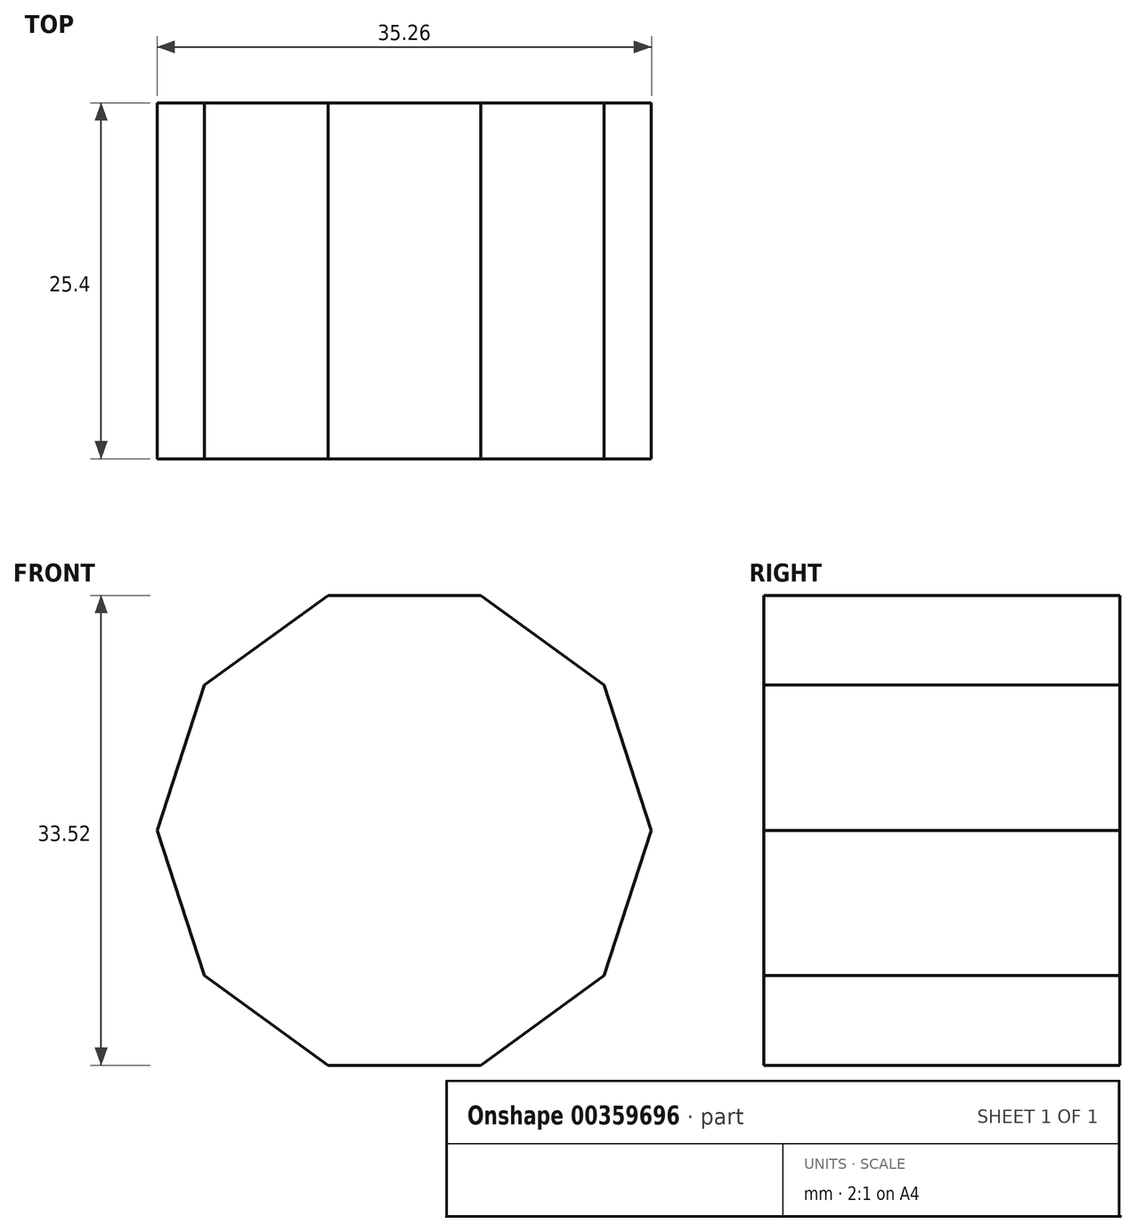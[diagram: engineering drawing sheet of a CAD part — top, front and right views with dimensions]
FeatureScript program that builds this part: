
annotation { "Feature Type Name" : "Feature", "Feature Type Description" : "" }
export const myFeature = defineFeature(function(context is Context, id is Id, definition is map)
    precondition{}
    {
        {
            var Q0;
            Q0=qCreatedBy(makeId("Front.planeOp"),FACE);
            var sketch = newSketch(context, id + "F0", { "sketchPlane" : qUnion([Q0])});
            skLineSegment(sketch, "E0", {"start": v(0, 0) * mm, "end": v(0, 16.76) * mm});
            skCircle(sketch, "E1.cCircle", {"center": v(0, 0) * mm, "radius": 16.76 * mm, "construction": true});
            skLineSegment(sketch, "E1.0", {"start": v(-5.45, 16.76) * mm, "end": v(5.45, 16.76) * mm});
            skLineSegment(sketch, "E1.1", {"start": v(5.45, 16.76) * mm, "end": v(14.26, 10.36) * mm});
            skLineSegment(sketch, "E1.2", {"start": v(14.26, 10.36) * mm, "end": v(17.63, 0) * mm});
            skLineSegment(sketch, "E1.3", {"start": v(17.63, 0) * mm, "end": v(14.26, -10.36) * mm});
            skLineSegment(sketch, "E1.4", {"start": v(14.26, -10.36) * mm, "end": v(5.45, -16.76) * mm});
            skLineSegment(sketch, "E1.5", {"start": v(5.45, -16.76) * mm, "end": v(-5.45, -16.76) * mm});
            skLineSegment(sketch, "E1.6", {"start": v(-5.45, -16.76) * mm, "end": v(-14.26, -10.36) * mm});
            skLineSegment(sketch, "E1.7", {"start": v(-14.26, -10.36) * mm, "end": v(-17.63, 0) * mm});
            skLineSegment(sketch, "E1.8", {"start": v(-17.63, 0) * mm, "end": v(-14.26, 10.36) * mm});
            skLineSegment(sketch, "E1.9", {"start": v(-14.26, 10.36) * mm, "end": v(-5.45, 16.76) * mm});
            skPoint(sketch, "E1.0.midPoint", {"position": v(0, 16.76) * mm});
            skSolve(sketch);
        }
        {
            var Q0;
            {var subQ3=sQuery(id+"F0.wireOp",EDGE,"E1.1");Q0=makeQuery(id+"F0.imprint","IMPRINT",FACE,{"disambiguationData":[TD([[makeQuery(id+"F0.imprint","IMPRINT",EDGE,{"derivedFrom":subQ3}),-1.0]])]});}
            extrude(context, id + "F1", {"entities" : qUnion([Q0]), "depth" : 25.4 * mm});
        }
    });
